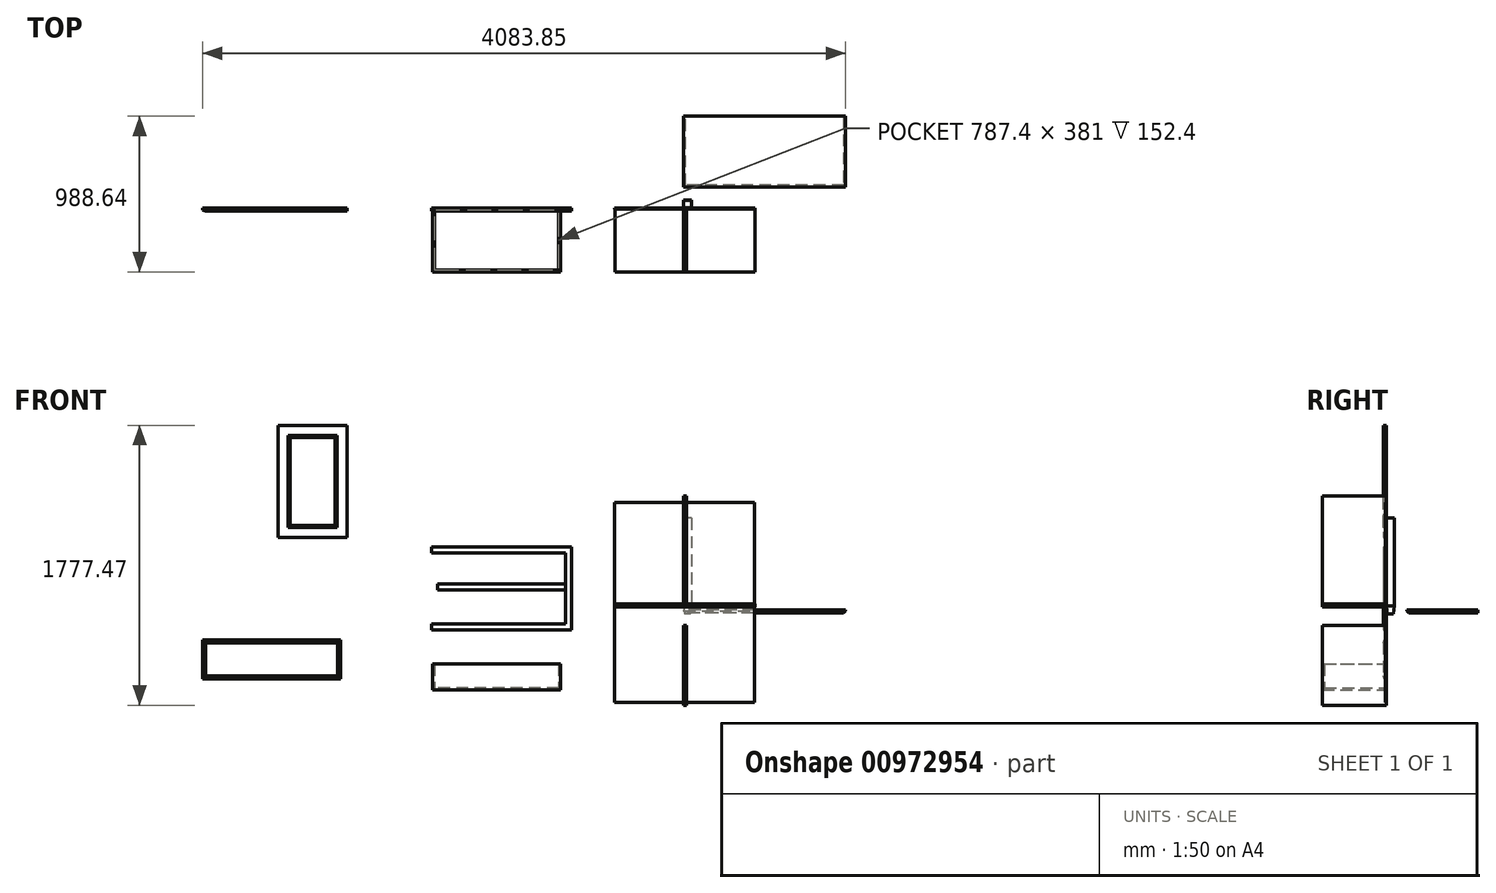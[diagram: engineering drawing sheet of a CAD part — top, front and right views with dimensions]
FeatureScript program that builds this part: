
annotation { "Feature Type Name" : "Feature", "Feature Type Description" : "" }
export const myFeature = defineFeature(function(context is Context, id is Id, definition is map)
    precondition{}
    {
        {
            var Q0;
            Q0=qCreatedBy(makeId("Front.planeOp"),FACE);
            var sketch = newSketch(context, id + "F0", { "sketchPlane" : qUnion([Q0])});
            skLineSegment(sketch, "E0.bottom", {"start": v(449.97, -608.9) * mm, "end": v(-439.03, -608.9) * mm});
            skLineSegment(sketch, "E0.top", {"start": v(449.97, 661.1) * mm, "end": v(-439.03, 661.1) * mm});
            skLineSegment(sketch, "E0.left", {"start": v(449.97, -608.9) * mm, "end": v(449.97, 661.1) * mm});
            skLineSegment(sketch, "E0.right", {"start": v(-439.03, -608.9) * mm, "end": v(-439.03, 661.1) * mm});
            skPoint(sketch, "E0.middle", {"position": v(5.47, 26.1) * mm});
            skSolve(sketch);
        }
        {
            var Q0;
            Q0=makeQuery(id+"F0.imprint","IMPRINT",FACE,{"disambiguationData":[TD([[makeQuery(id+"F0.imprint","IMPRINT",EDGE,{"derivedFrom":sQuery(id+"F0.wireOp",EDGE,"E0.bottom")}),-1.0]])]});
            extrude(context, id + "F1", {"entities" : qUnion([Q0]), "depth" : 6.35 * mm, "offsetDistance" : 25.4 * mm});
        }
        {
            var Q0;
            Q0=qCreatedBy(makeId("Right.planeOp"),FACE);
            var sketch = newSketch(context, id + "F2", { "sketchPlane" : qUnion([Q0])});
            skLineSegment(sketch, "E1.bottom", {"start": v(0, -117.64) * mm, "end": v(-406.4, -117.64) * mm});
            skLineSegment(sketch, "E1.top", {"start": v(0, -625.64) * mm, "end": v(-406.4, -625.64) * mm});
            skLineSegment(sketch, "E1.left", {"start": v(0, -117.64) * mm, "end": v(0, -625.64) * mm});
            skLineSegment(sketch, "E1.right", {"start": v(-406.4, -117.64) * mm, "end": v(-406.4, -625.64) * mm});
            skSolve(sketch);
        }
        {
            var Q0;
            Q0=makeQuery(id+"F2.imprint","IMPRINT",FACE,{"disambiguationData":[TD([[makeQuery(id+"F2.imprint","IMPRINT",EDGE,{"derivedFrom":sQuery(id+"F2.wireOp",EDGE,"E1.bottom")}),1.0]])]});
            extrude(context, id + "F3", {"entities" : qUnion([Q0]), "depth" : 19.05 * mm, "offsetDistance" : 25.4 * mm});
        }
        {
            var Q0;
            Q0=qCreatedBy(makeId("Top.planeOp"),FACE);
            var sketch = newSketch(context, id + "F4", { "sketchPlane" : qUnion([Q0])});
            skLineSegment(sketch, "E2.bottom", {"start": v(-436.3, 0) * mm, "end": v(452.7, 0) * mm});
            skLineSegment(sketch, "E2.top", {"start": v(-436.3, -406.4) * mm, "end": v(452.7, -406.4) * mm});
            skLineSegment(sketch, "E2.left", {"start": v(-436.3, 0) * mm, "end": v(-436.3, -406.4) * mm});
            skLineSegment(sketch, "E2.right", {"start": v(452.7, 0) * mm, "end": v(452.7, -406.4) * mm});
            skSolve(sketch);
        }
        {
            var Q0;
            Q0=makeQuery(id+"F4.imprint","IMPRINT",FACE,{"disambiguationData":[TD([[makeQuery(id+"F4.imprint","IMPRINT",EDGE,{"derivedFrom":sQuery(id+"F4.wireOp",EDGE,"E2.bottom")}),-1.0]])]});
            extrude(context, id + "F5", {"entities" : qUnion([Q0]), "depth" : 19.05 * mm, "offsetDistance" : 25.4 * mm});
        }
        {
            var Q0;
            Q0=qCreatedBy(makeId("Right.planeOp"),FACE);
            var sketch = newSketch(context, id + "F6", { "sketchPlane" : qUnion([Q0])});
            skLineSegment(sketch, "E3.bottom", {"start": v(0, 562.4) * mm, "end": v(50.8, 562.4) * mm});
            skLineSegment(sketch, "E3.top", {"start": v(0, -47.2) * mm, "end": v(50.8, -47.2) * mm});
            skLineSegment(sketch, "E3.left", {"start": v(0, 562.4) * mm, "end": v(0, -47.2) * mm});
            skLineSegment(sketch, "E3.right", {"start": v(50.8, 562.4) * mm, "end": v(50.8, -47.2) * mm});
            skSolve(sketch);
        }
        {
            var Q0;
            Q0=makeQuery(id+"F6.imprint","IMPRINT",FACE,{"disambiguationData":[TD([[makeQuery(id+"F6.imprint","IMPRINT",EDGE,{"derivedFrom":sQuery(id+"F6.wireOp",EDGE,"E3.bottom")}),-1.0]])]});
            var Q1;
            Q1=makeQuery(id+"F6.imprint","IMPRINT",FACE,{"disambiguationData":[TD([[makeQuery(id+"F6.imprint","IMPRINT",EDGE,{"derivedFrom":sQuery(id+"F6.wireOp",EDGE,"E3.top")}),-1.0]])]});
            extrude(context, id + "F7", {"entities" : qUnion([Q0, Q1]), "depth" : 50.8 * mm, "offsetDistance" : 25.4 * mm});
        }
        {
            var Q0;
            Q0=makeQuery(id+"F7.opExtrude","CAP_EDGE",EDGE,{"disambiguationData":[OSD([sQuery(id+"F6.wireOp",EDGE,"E3.top")])],"isStart":false});
            var Q1;
            Q1=makeQuery(id+"F7.opExtrude","SWEPT_EDGE",EDGE,{"disambiguationData":[OSD([sQuery(id+"F6.wireOp",EDGE,"E3.top"),sQuery(id+"F6.wireOp",EDGE,"E3.right")])]});
            var Q2;
            Q2=makeQuery(id+"F7.opExtrude","CAP_EDGE",EDGE,{"disambiguationData":[OSD([sQuery(id+"F6.wireOp",EDGE,"E3.top")])],"isStart":true});
            var Q3;
            Q3=makeQuery(id+"F7.opExtrude","SWEPT_EDGE",EDGE,{"disambiguationData":[OSD([sQuery(id+"F6.wireOp",EDGE,"E3.top"),sQuery(id+"F6.wireOp",EDGE,"E3.left")])]});
            chamfer(context, id + "F8", {"entities" : qUnion([Q0, Q1, Q2, Q3]), "chamferType" : ChamferType.TWO_OFFSETS, "width1" : 50.8 * mm, "oppositeDirection" : false, "width2" : 6.35 * mm, "tangentPropagation" : true});
        }
        {
            var Q0;
            Q0=qCreatedBy(makeId("Right.planeOp"),FACE);
            var sketch = newSketch(context, id + "F9", { "sketchPlane" : qUnion([Q0])});
            skLineSegment(sketch, "E4.bottom", {"start": v(131.4, -19.29) * mm, "end": v(582.24, -19.29) * mm});
            skLineSegment(sketch, "E4.top", {"start": v(131.4, -38.34) * mm, "end": v(582.24, -38.34) * mm});
            skLineSegment(sketch, "E4.left", {"start": v(131.4, -19.29) * mm, "end": v(131.4, -38.34) * mm});
            skLineSegment(sketch, "E4.right", {"start": v(582.24, -19.29) * mm, "end": v(582.24, -38.34) * mm});
            skSolve(sketch);
        }
        {
            var Q0;
            Q0 = qSketchRegion(id + "F9", true);
            extrude(context, id + "F10", {"entities" : qUnion([Q0]), "depth" : 1028.7 * mm, "offsetDistance" : 25.4 * mm});
        }
        {
            var Q0;
            Q0=makeQuery(id+"F10.opExtrude","CAP_EDGE",EDGE,{"disambiguationData":[OSD([sQuery(id+"F9.wireOp",EDGE,"E4.top")])],"isStart":false});
            var Q1;
            Q1=makeQuery(id+"F10.opExtrude","SWEPT_EDGE",EDGE,{"disambiguationData":[OSD([sQuery(id+"F9.wireOp",EDGE,"E4.top"),sQuery(id+"F9.wireOp",EDGE,"E4.left")])]});
            var Q2;
            Q2=makeQuery(id+"F10.opExtrude","CAP_EDGE",EDGE,{"disambiguationData":[OSD([sQuery(id+"F9.wireOp",EDGE,"E4.top")])],"isStart":true});
            chamfer(context, id + "F11", {"entities" : qUnion([Q0, Q1, Q2]), "width" : 12.7 * mm, "tangentPropagation" : true});
        }
        {
            var Q0;
            Q0=qCreatedBy(makeId("Right.planeOp"),FACE);
            var sketch = newSketch(context, id + "F12", { "sketchPlane" : qUnion([Q0])});
            skLineSegment(sketch, "E5.bottom", {"start": v(0, 704.85) * mm, "end": v(-406.4, 704.85) * mm});
            skLineSegment(sketch, "E5.top", {"start": v(0, 0) * mm, "end": v(-406.4, 0) * mm});
            skLineSegment(sketch, "E5.left", {"start": v(0, 704.85) * mm, "end": v(0, 0) * mm});
            skLineSegment(sketch, "E5.right", {"start": v(-406.4, 704.85) * mm, "end": v(-406.4, 0) * mm});
            skSolve(sketch);
        }
        {
            var Q0;
            Q0=makeQuery(id+"F12.imprint","IMPRINT",FACE,{"disambiguationData":[TD([[makeQuery(id+"F12.imprint","IMPRINT",EDGE,{"derivedFrom":sQuery(id+"F12.wireOp",EDGE,"E5.bottom")}),1.0]])]});
            extrude(context, id + "F13", {"entities" : qUnion([Q0]), "depth" : 19.05 * mm, "offsetDistance" : 25.4 * mm});
        }
        {
            var Q0;
            Q0=qCreatedBy(makeId("Front.planeOp"),FACE);
            var sketch = newSketch(context, id + "F14", { "sketchPlane" : qUnion([Q0])});
            skLineSegment(sketch, "E6.bottom", {"start": v(-1601.16, 378.38) * mm, "end": v(-712.16, 378.38) * mm});
            skLineSegment(sketch, "E6.top", {"start": v(-1601.16, 340.28) * mm, "end": v(-712.16, 340.28) * mm});
            skLineSegment(sketch, "E6.left", {"start": v(-1601.16, 378.38) * mm, "end": v(-1601.16, 340.28) * mm});
            skLineSegment(sketch, "E6.right", {"start": v(-712.16, 378.38) * mm, "end": v(-712.16, 340.28) * mm});
            skLineSegment(sketch, "E7.bottom", {"start": v(-1601.16, 340.28) * mm, "end": v(-1563.06, 340.28) * mm});
            skLineSegment(sketch, "E7.top", {"start": v(-1601.16, -110.57) * mm, "end": v(-1563.06, -110.57) * mm});
            skLineSegment(sketch, "E7.left", {"start": v(-1601.16, 340.28) * mm, "end": v(-1601.16, -110.57) * mm});
            skLineSegment(sketch, "E7.right", {"start": v(-1563.06, 340.28) * mm, "end": v(-1563.06, -110.57) * mm});
            skLineSegment(sketch, "E8.bottom", {"start": v(-1601.16, -110.57) * mm, "end": v(-712.16, -110.57) * mm});
            skLineSegment(sketch, "E8.top", {"start": v(-1601.16, -148.67) * mm, "end": v(-712.16, -148.67) * mm});
            skLineSegment(sketch, "E8.left", {"start": v(-1601.16, -110.57) * mm, "end": v(-1601.16, -148.67) * mm});
            skLineSegment(sketch, "E8.right", {"start": v(-712.16, -110.57) * mm, "end": v(-712.16, -148.67) * mm});
            skLineSegment(sketch, "E9.bottom", {"start": v(-1562.94, 143.43) * mm, "end": v(-750.14, 143.43) * mm});
            skLineSegment(sketch, "E9.top", {"start": v(-1562.94, 105.33) * mm, "end": v(-750.14, 105.33) * mm});
            skLineSegment(sketch, "E9.left", {"start": v(-1562.94, 143.43) * mm, "end": v(-1562.94, 105.33) * mm});
            skLineSegment(sketch, "E9.right", {"start": v(-750.14, 143.43) * mm, "end": v(-750.14, 105.33) * mm});
            skLineSegment(sketch, "E10.bottom", {"start": v(-712.16, 340.28) * mm, "end": v(-750.26, 340.28) * mm});
            skLineSegment(sketch, "E10.top", {"start": v(-712.16, -110.57) * mm, "end": v(-750.26, -110.57) * mm});
            skLineSegment(sketch, "E10.left", {"start": v(-712.16, 340.28) * mm, "end": v(-712.16, -110.57) * mm});
            skLineSegment(sketch, "E10.right", {"start": v(-750.26, 340.28) * mm, "end": v(-750.26, -110.57) * mm});
            skSolve(sketch);
        }
        {
            var Q0;
            Q0=makeQuery(id+"F14.imprint","IMPRINT",FACE,{"disambiguationData":[TD([[makeQuery(id+"F14.imprint","IMPRINT",EDGE,{"derivedFrom":sQuery(id+"F14.wireOp",EDGE,"E6.bottom")}),-1.0]])]});
            var Q1;
            Q1=makeQuery(id+"F14.imprint","IMPRINT",FACE,{"disambiguationData":[TD([[makeQuery(id+"F14.imprint","IMPRINT",EDGE,{"derivedFrom":sQuery(id+"F14.wireOp",EDGE,"E7.bottom")}),-1.0]])]});
            var Q2;
            Q2=makeQuery(id+"F14.imprint","IMPRINT",FACE,{"disambiguationData":[TD([[makeQuery(id+"F14.imprint","IMPRINT",EDGE,{"derivedFrom":sQuery(id+"F14.wireOp",EDGE,"E8.top")}),1.0]])]});
            var Q3;
            {var subQ0=sQuery(id+"F14.wireOp",EDGE,"E9.right");Q3=makeQuery(id+"F14.imprint","IMPRINT",FACE,{"disambiguationData":[TD([[makeQuery(id+"F14.imprint","IMPRINT",EDGE,{"derivedFrom":subQ0}),1.0]])]});}
            var Q4;
            {var subQ0=sQuery(id+"F14.wireOp",EDGE,"E9.left");Q4=makeQuery(id+"F14.imprint","IMPRINT",FACE,{"disambiguationData":[TD([[makeQuery(id+"F14.imprint","IMPRINT",EDGE,{"derivedFrom":subQ0}),1.0]])]});}
            extrude(context, id + "F15", {"entities" : qUnion([Q0, Q1, Q2, Q3, Q4]), "depth" : 19.05 * mm, "offsetDistance" : 25.4 * mm});
        }
        {
            var Q0;
            Q0=qCreatedBy(makeId("Front.planeOp"),FACE);
            var sketch = newSketch(context, id + "F16", { "sketchPlane" : qUnion([Q0])});
            skLineSegment(sketch, "E11.bottom", {"start": v(-780.76, -528.77) * mm, "end": v(-1593.56, -528.77) * mm});
            skLineSegment(sketch, "E11.top", {"start": v(-780.76, -516.07) * mm, "end": v(-1593.56, -516.07) * mm});
            skLineSegment(sketch, "E11.left", {"start": v(-780.76, -528.77) * mm, "end": v(-780.76, -516.07) * mm});
            skLineSegment(sketch, "E11.right", {"start": v(-1593.56, -528.77) * mm, "end": v(-1593.56, -516.07) * mm});
            skPoint(sketch, "E11.middle", {"position": v(-1187.16, -522.42) * mm});
            skSolve(sketch);
        }
        {
            var Q0;
            Q0=makeQuery(id+"F16.imprint","IMPRINT",FACE,{"disambiguationData":[TD([[makeQuery(id+"F16.imprint","IMPRINT",EDGE,{"derivedFrom":sQuery(id+"F16.wireOp",EDGE,"E11.bottom")}),-1.0]])]});
            extrude(context, id + "F17", {"entities" : qUnion([Q0]), "depth" : 406.4 * mm, "offsetDistance" : 25.4 * mm});
        }
        {
            var Q0;
            Q0=makeQuery(id+"F17.opExtrude","SWEPT_FACE",FACE,{"disambiguationData":[OSD([sQuery(id+"F16.wireOp",EDGE,"E11.top")])]});
            var sketch = newSketch(context, id + "F18", { "sketchPlane" : qUnion([Q0])});
            skLineSegment(sketch, "E12.0", {"start": v(-780.76, -393.7) * mm, "end": v(-1593.56, -393.7) * mm});
            skLineSegment(sketch, "E13.0", {"start": v(-793.46, -406.4) * mm, "end": v(-793.46, 0) * mm});
            skLineSegment(sketch, "E14.0", {"start": v(-780.76, -12.7) * mm, "end": v(-1593.56, -12.7) * mm});
            skLineSegment(sketch, "E15.0", {"start": v(-1580.86, -406.4) * mm, "end": v(-1580.86, 0) * mm});
            skSolve(sketch);
        }
        {
            var Q0;
            {var subQ0=sQuery(id+"F18.wireOp",EDGE,"E13.0");var subQ1=makeQuery(id+"F17.opExtrude","CAP_EDGE",EDGE,{"disambiguationData":[OSD([sQuery(id+"F16.wireOp",EDGE,"E11.top")])],"isStart":true});var subQ2=makeQuery(id+"F18.imprint","INTERSECT",VERTEX,{"derivedFrom":[subQ1,subQ0]});Q0=makeQuery(id+"F18.imprint","IMPRINT",FACE,{"disambiguationData":[TD([[makeQuery(id+"F18.imprint","IMPRINT",EDGE,{"disambiguationData":[TD([[subQ2,1.0]])],"derivedFrom":subQ0}),1.0]])]});}
            var Q1;
            {var subQ0=sQuery(id+"F18.wireOp",EDGE,"E12.0");var subQ3=sQuery(id+"F18.wireOp",EDGE,"E13.0");var subQ4=makeQuery(id+"F18.imprint","INTERSECT",VERTEX,{"derivedFrom":[subQ0,subQ3]});Q1=makeQuery(id+"F18.imprint","IMPRINT",FACE,{"disambiguationData":[TD([[makeQuery(id+"F18.imprint","IMPRINT",EDGE,{"disambiguationData":[TD([[subQ4,-1.0]])],"derivedFrom":subQ3}),-1.0]])]});}
            var Q2;
            {var subQ0=sQuery(id+"F18.wireOp",EDGE,"E13.0");var subQ1=sQuery(id+"F18.wireOp",EDGE,"E12.0");var subQ2=makeQuery(id+"F18.imprint","INTERSECT",VERTEX,{"derivedFrom":[subQ1,subQ0]});Q2=makeQuery(id+"F18.imprint","IMPRINT",FACE,{"disambiguationData":[TD([[makeQuery(id+"F18.imprint","IMPRINT",EDGE,{"disambiguationData":[TD([[subQ2,-1.0]])],"derivedFrom":subQ1}),1.0]])]});}
            var Q3;
            {var subQ0=sQuery(id+"F18.wireOp",EDGE,"E12.0");var subQ3=sQuery(id+"F18.wireOp",EDGE,"E15.0");var subQ4=makeQuery(id+"F18.imprint","INTERSECT",VERTEX,{"derivedFrom":[subQ0,subQ3]});Q3=makeQuery(id+"F18.imprint","IMPRINT",FACE,{"disambiguationData":[TD([[makeQuery(id+"F18.imprint","IMPRINT",EDGE,{"disambiguationData":[TD([[subQ4,-1.0]])],"derivedFrom":subQ3}),1.0]])]});}
            var Q4;
            {var subQ0=sQuery(id+"F18.wireOp",EDGE,"E13.0");var subQ1=sQuery(id+"F16.wireOp",EDGE,"E11.top");var subQ2=makeQuery(id+"F17.opExtrude","CAP_EDGE",EDGE,{"disambiguationData":[OSD([subQ1])],"isStart":true});var subQ3=makeQuery(id+"F18.imprint","INTERSECT",VERTEX,{"derivedFrom":[subQ2,subQ0]});Q4=makeQuery(id+"F18.imprint","IMPRINT",FACE,{"disambiguationData":[TD([[makeQuery(id+"F18.imprint","IMPRINT",EDGE,{"disambiguationData":[TD([[subQ3,1.0]])],"derivedFrom":subQ0}),-1.0]])]});}
            var Q5;
            {var subQ1=sQuery(id+"F16.wireOp",EDGE,"E11.top");var subQ4=sQuery(id+"F18.wireOp",EDGE,"E13.0");var subQ6=makeQuery(id+"F17.opExtrude","CAP_EDGE",EDGE,{"disambiguationData":[OSD([subQ1])],"isStart":false});var subQ7=makeQuery(id+"F18.imprint","INTERSECT",VERTEX,{"derivedFrom":[subQ6,subQ4]});Q5=makeQuery(id+"F18.imprint","IMPRINT",FACE,{"disambiguationData":[TD([[makeQuery(id+"F18.imprint","IMPRINT",EDGE,{"disambiguationData":[TD([[subQ7,-1.0]])],"derivedFrom":subQ4}),-1.0]])]});}
            var Q6;
            {var subQ1=sQuery(id+"F16.wireOp",EDGE,"E11.top");var subQ4=sQuery(id+"F18.wireOp",EDGE,"E15.0");var subQ6=makeQuery(id+"F17.opExtrude","CAP_EDGE",EDGE,{"disambiguationData":[OSD([subQ1])],"isStart":false});var subQ8=makeQuery(id+"F18.imprint","INTERSECT",VERTEX,{"derivedFrom":[subQ6,subQ4]});Q6=makeQuery(id+"F18.imprint","IMPRINT",FACE,{"disambiguationData":[TD([[makeQuery(id+"F18.imprint","IMPRINT",EDGE,{"disambiguationData":[TD([[subQ8,-1.0]])],"derivedFrom":subQ4}),1.0]])]});}
            var Q7;
            {var subQ1=sQuery(id+"F16.wireOp",EDGE,"E11.top");var subQ4=sQuery(id+"F18.wireOp",EDGE,"E15.0");var subQ6=makeQuery(id+"F17.opExtrude","CAP_EDGE",EDGE,{"disambiguationData":[OSD([subQ1])],"isStart":true});var subQ7=makeQuery(id+"F18.imprint","INTERSECT",VERTEX,{"derivedFrom":[subQ6,subQ4]});Q7=makeQuery(id+"F18.imprint","IMPRINT",FACE,{"disambiguationData":[TD([[makeQuery(id+"F18.imprint","IMPRINT",EDGE,{"disambiguationData":[TD([[subQ7,1.0]])],"derivedFrom":subQ4}),1.0]])]});}
            extrude(context, id + "F19", {"entities" : qUnion([Q0, Q1, Q2, Q3, Q4, Q5, Q6, Q7]), "operationType" : NewBodyOperationType.ADD, "depth" : 152.4 * mm, "offsetDistance" : 25.4 * mm});
        }
        {
            var Q0;
            Q0=qCreatedBy(makeId("Front.planeOp"),FACE);
            var sketch = newSketch(context, id + "F20", { "sketchPlane" : qUnion([Q0])});
            skLineSegment(sketch, "E16.bottom", {"start": v(-2178.85, -456.8) * mm, "end": v(-3055.15, -456.8) * mm});
            skLineSegment(sketch, "E16.top", {"start": v(-2178.85, -209.15) * mm, "end": v(-3055.15, -209.15) * mm});
            skLineSegment(sketch, "E16.left", {"start": v(-2178.85, -456.8) * mm, "end": v(-2178.85, -209.15) * mm});
            skLineSegment(sketch, "E16.right", {"start": v(-3055.15, -456.8) * mm, "end": v(-3055.15, -209.15) * mm});
            skPoint(sketch, "E16.middle", {"position": v(-2617, -332.97) * mm});
            skSolve(sketch);
        }
        {
            var Q0;
            Q0=makeQuery(id+"F20.imprint","IMPRINT",FACE,{"disambiguationData":[TD([[makeQuery(id+"F20.imprint","IMPRINT",EDGE,{"derivedFrom":sQuery(id+"F20.wireOp",EDGE,"E16.bottom")}),-1.0]])]});
            extrude(context, id + "F21", {"entities" : qUnion([Q0]), "depth" : 19.05 * mm, "offsetDistance" : 25.4 * mm});
        }
        {
            var Q0;
            Q0=makeQuery(id+"F21.opExtrude","CAP_EDGE",EDGE,{"disambiguationData":[OSD([sQuery(id+"F20.wireOp",EDGE,"E16.top")])],"isStart":false});
            var Q1;
            Q1=makeQuery(id+"F21.opExtrude","CAP_EDGE",EDGE,{"disambiguationData":[OSD([sQuery(id+"F20.wireOp",EDGE,"E16.left")])],"isStart":false});
            var Q2;
            Q2=makeQuery(id+"F21.opExtrude","CAP_EDGE",EDGE,{"disambiguationData":[OSD([sQuery(id+"F20.wireOp",EDGE,"E16.bottom")])],"isStart":false});
            var Q3;
            Q3=makeQuery(id+"F21.opExtrude","CAP_EDGE",EDGE,{"disambiguationData":[OSD([sQuery(id+"F20.wireOp",EDGE,"E16.right")])],"isStart":false});
            chamfer(context, id + "F22", {"entities" : qUnion([Q0, Q1, Q2, Q3]), "chamferType" : ChamferType.TWO_OFFSETS, "width1" : 19.05 * mm, "oppositeDirection" : false, "width2" : 6.35 * mm, "tangentPropagation" : true});
        }
        {
            var Q0;
            Q0=qCreatedBy(makeId("Front.planeOp"),FACE);
            var sketch = newSketch(context, id + "F23", { "sketchPlane" : qUnion([Q0])});
            skLineSegment(sketch, "E17.bottom", {"start": v(-2575.8, 1151.83) * mm, "end": v(-2137.65, 1151.83) * mm});
            skLineSegment(sketch, "E17.top", {"start": v(-2575.8, 440.63) * mm, "end": v(-2137.65, 440.63) * mm});
            skLineSegment(sketch, "E17.left", {"start": v(-2575.8, 1151.83) * mm, "end": v(-2575.8, 440.63) * mm});
            skLineSegment(sketch, "E17.right", {"start": v(-2137.65, 1151.83) * mm, "end": v(-2137.65, 440.63) * mm});
            skLineSegment(sketch, "E18.0", {"start": v(-2213.85, 1075.63) * mm, "end": v(-2213.85, 516.83) * mm});
            skLineSegment(sketch, "E18.1", {"start": v(-2499.6, 1075.63) * mm, "end": v(-2213.85, 1075.63) * mm});
            skLineSegment(sketch, "E18.2", {"start": v(-2499.6, 1075.63) * mm, "end": v(-2499.6, 516.83) * mm});
            skLineSegment(sketch, "E18.3", {"start": v(-2499.6, 516.83) * mm, "end": v(-2213.85, 516.83) * mm});
            skSolve(sketch);
        }
        {
            var Q0;
            Q0=makeQuery(id+"F23.imprint","IMPRINT",FACE,{"disambiguationData":[TD([[makeQuery(id+"F23.imprint","IMPRINT",EDGE,{"derivedFrom":sQuery(id+"F23.wireOp",EDGE,"E17.bottom")}),-1.0]])]});
            extrude(context, id + "F24", {"entities" : qUnion([Q0]), "depth" : 19.05 * mm, "offsetDistance" : 25.4 * mm});
        }
        {
            var Q0;
            Q0=makeQuery(id+"F24.opExtrude","CAP_EDGE",EDGE,{"disambiguationData":[OSD([sQuery(id+"F23.wireOp",EDGE,"E18.2")])],"isStart":false});
            var Q1;
            Q1=makeQuery(id+"F24.opExtrude","CAP_EDGE",EDGE,{"disambiguationData":[OSD([sQuery(id+"F23.wireOp",EDGE,"E18.1")])],"isStart":false});
            var Q2;
            Q2=makeQuery(id+"F24.opExtrude","CAP_EDGE",EDGE,{"disambiguationData":[OSD([sQuery(id+"F23.wireOp",EDGE,"E18.0")])],"isStart":false});
            var Q3;
            Q3=makeQuery(id+"F24.opExtrude","CAP_EDGE",EDGE,{"disambiguationData":[OSD([sQuery(id+"F23.wireOp",EDGE,"E18.3")])],"isStart":false});
            chamfer(context, id + "F25", {"entities" : qUnion([Q0, Q1, Q2, Q3]), "width" : 12.7 * mm, "tangentPropagation" : true});
        }
        {
            var Q0;
            Q0=qCreatedBy(makeId("Front.planeOp"),FACE);
            var sketch = newSketch(context, id + "F26", { "sketchPlane" : qUnion([Q0])});
            skLineSegment(sketch, "E19.0", {"start": v(-2499.6, 1075.63) * mm, "end": v(-2499.6, 516.83) * mm});
            skLineSegment(sketch, "E20.0", {"start": v(-2499.6, 1075.63) * mm, "end": v(-2213.85, 1075.63) * mm});
            skLineSegment(sketch, "E21.0", {"start": v(-2213.85, 1075.63) * mm, "end": v(-2213.85, 516.83) * mm});
            skLineSegment(sketch, "E22.0", {"start": v(-2499.6, 516.83) * mm, "end": v(-2213.85, 516.83) * mm});
            skSolve(sketch);
        }
        {
            var Q0;
            Q0=makeQuery(id+"F26.imprint","IMPRINT",FACE,{"disambiguationData":[TD([[makeQuery(id+"F26.imprint","IMPRINT",EDGE,{"derivedFrom":sQuery(id+"F26.wireOp",EDGE,"E19.0")}),1.0]])]});
            extrude(context, id + "F27", {"entities" : qUnion([Q0]), "operationType" : NewBodyOperationType.ADD, "depth" : 6.35 * mm, "offsetDistance" : 25.4 * mm});
        }
    });
